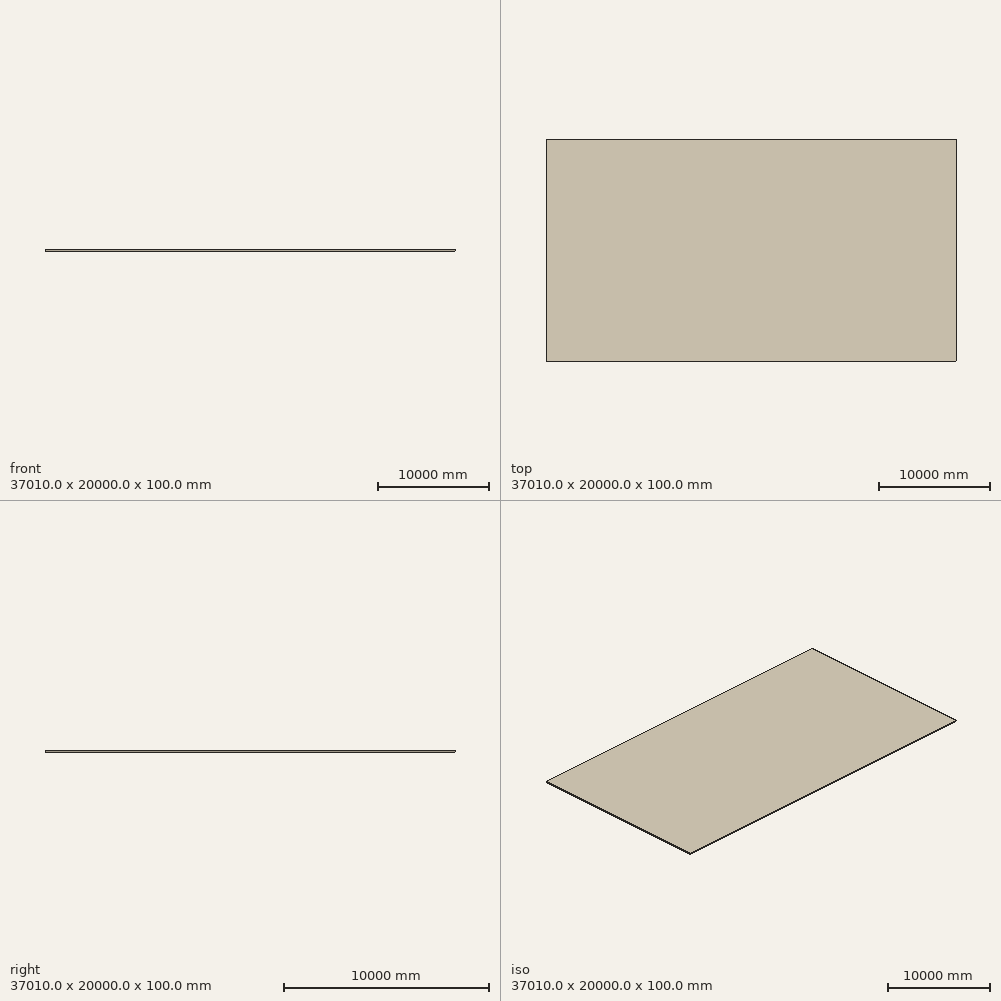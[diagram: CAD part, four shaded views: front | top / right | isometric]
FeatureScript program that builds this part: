
annotation { "Feature Type Name" : "Feature", "Feature Type Description" : "" }
export const myFeature = defineFeature(function(context is Context, id is Id, definition is map)
    precondition{}
    {
        {
            var Q0;
            Q0=qCreatedBy(makeId("Top.planeOp"),FACE);
            var sketch = newSketch(context, id + "F0", { "sketchPlane" : qUnion([Q0])});
            skLineSegment(sketch, "E0.bottom", {"start": v(18505, -10000) * mm, "end": v(-18505, -10000) * mm});
            skLineSegment(sketch, "E0.top", {"start": v(18505, 10000) * mm, "end": v(-18505, 10000) * mm});
            skLineSegment(sketch, "E0.left", {"start": v(18505, -10000) * mm, "end": v(18505, 10000) * mm});
            skLineSegment(sketch, "E0.right", {"start": v(-18505, -10000) * mm, "end": v(-18505, 10000) * mm});
            skPoint(sketch, "E0.middle", {"position": v(0, 0) * mm});
            skSolve(sketch);
        }
        {
            var Q0;
            Q0=makeQuery(id+"F0.imprint","IMPRINT",FACE,{"disambiguationData":[TD([[makeQuery(id+"F0.imprint","IMPRINT",EDGE,{"derivedFrom":sQuery(id+"F0.wireOp",EDGE,"E0.bottom")}),-1.0]])]});
            extrude(context, id + "F1", {"entities" : qUnion([Q0]), "oppositeDirection" : true, "depth" : 100 * mm, "offsetDistance" : 25 * mm});
        }
    });
